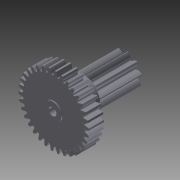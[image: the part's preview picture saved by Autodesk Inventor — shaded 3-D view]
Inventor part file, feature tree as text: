
AUTODESK INVENTOR PART (.ipt)
format: ipt  version: 2013 (Build 170138000, 138)  size: 1,575,936 bytes
history: native  units: in
note: dims shown in document units (in); Inventor stores cm internally (conversion verified against a paired STEP export)
features: extrude x6, sketch x6, fillet x2, pattern_circular x1
ambient origin geometry x8: Origin, YZ Plane, XZ Plane, XY Plane, X Axis, Y Axis, Z Axis, Center Point
bodies: Solid1 (feature_tree)
feature tree (15):
  extrude  "Extrusion1"  Depth=0.138in
  extrude  "Extrusion2"  Depth=0.256in
  extrude  "Extrusion3"  Depth=0.05in
  fillet  "Fillet1"  Radius=0.335in
  extrude  "Extrusion4"  Depth=3.937in TaperAngle=360.0deg
  fillet  "Fillet2"  Radius=0.148in
  pattern_circular  "Circular Pattern1"  [2 undecoded]
  extrude  "Extrusion5"  [1 undecoded]
  extrude  "Extrusion6"  [1 undecoded]
  sketch  "Sketch1"  dims[d0=0.118in d1=0.0in d2=0.138in]
  sketch  "Sketch2"  dims[d3=0.008in d4=0.0in d5=0.256in]
  sketch  "Sketch3"  dims[d6=0.118in d7=0.0in d8=0.05in d9=0.335in d10=0.0in]
  sketch  "Sketch4"  dims[d11=0.003in d12=3.937in d13=360.0deg d15=0.148in]
  sketch  "Sketch5"  dims[d16=0.008in d17=0.0in]
  sketch  "Sketch6"  dims[d18=0.061in d19=0.008in d20=0.0in]
note: 4 required parameter values undecoded (feature->parameter linkage not recoverable at this tier; creation-order binding heuristic only, values carry confidence <= 0.55)
